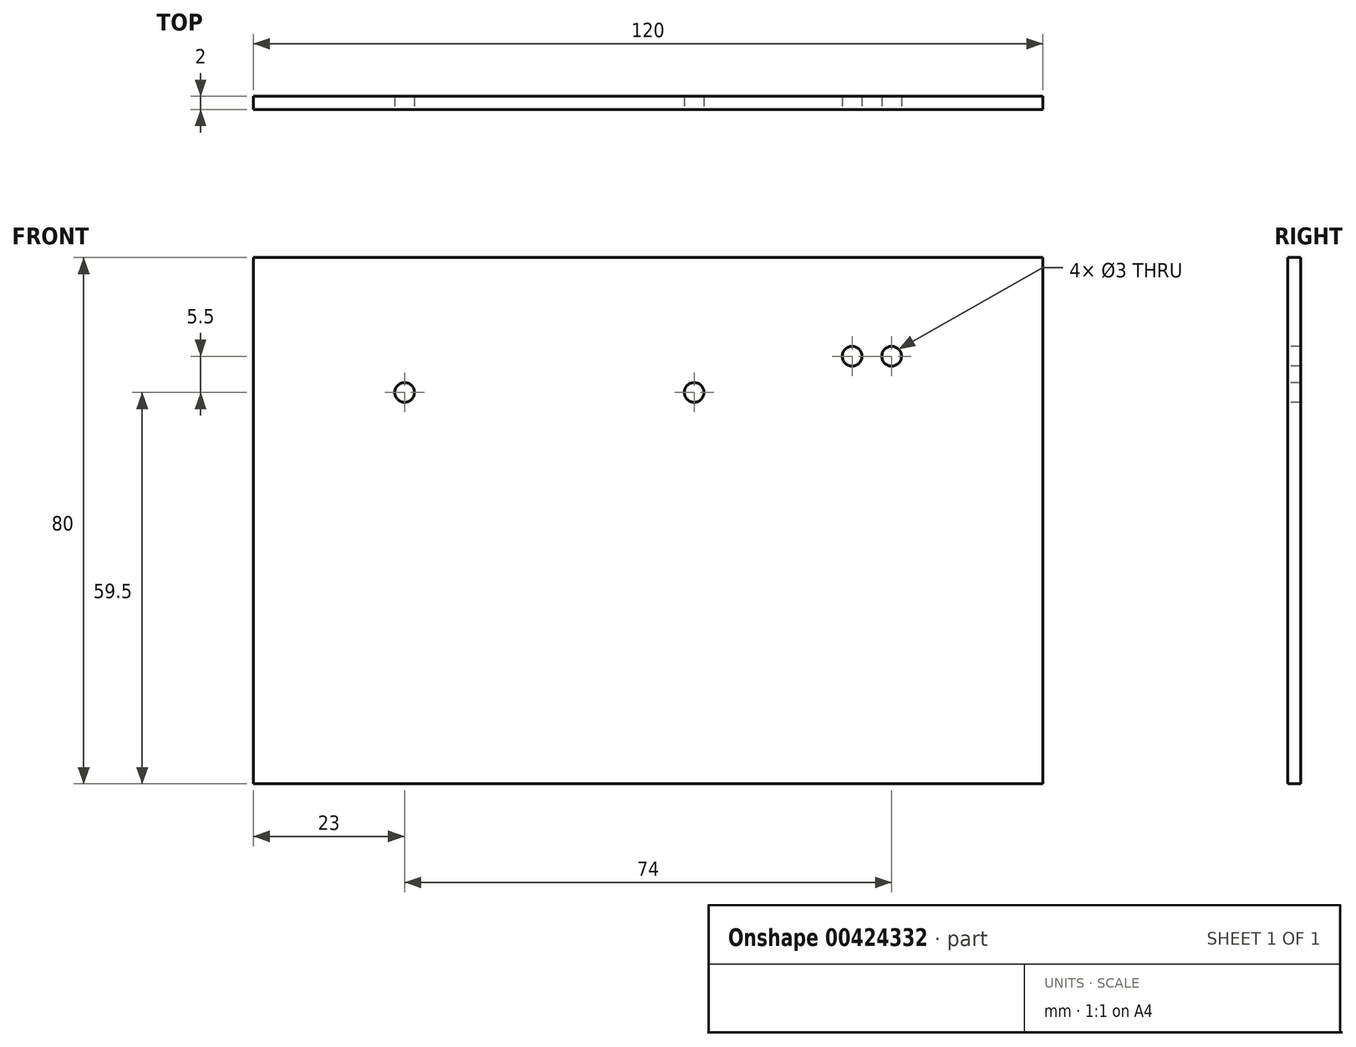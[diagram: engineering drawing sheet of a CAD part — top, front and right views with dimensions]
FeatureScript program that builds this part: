
annotation { "Feature Type Name" : "Feature", "Feature Type Description" : "" }
export const myFeature = defineFeature(function(context is Context, id is Id, definition is map)
    precondition{}
    {
        {
            var Q0;
            Q0=qCreatedBy(makeId("Front.planeOp"),FACE);
            var sketch = newSketch(context, id + "F0", { "sketchPlane" : qUnion([Q0])});
            skLineSegment(sketch, "E0.bottom", {"start": v(0, 0) * mm, "end": v(120, 0) * mm});
            skLineSegment(sketch, "E0.top", {"start": v(0, 80) * mm, "end": v(120, 80) * mm});
            skLineSegment(sketch, "E0.left", {"start": v(0, 0) * mm, "end": v(0, 80) * mm});
            skLineSegment(sketch, "E0.right", {"start": v(120, 0) * mm, "end": v(120, 80) * mm});
            skSolve(sketch);
        }
        {
            var Q0;
            Q0=makeQuery(id+"F0.imprint","IMPRINT",FACE,{"disambiguationData":[TD([[makeQuery(id+"F0.imprint","IMPRINT",EDGE,{"derivedFrom":sQuery(id+"F0.wireOp",EDGE,"E0.bottom")}),1.0]])]});
            extrude(context, id + "F1", {"entities" : qUnion([Q0]), "depth" : 2 * mm});
        }
        {
            var Q0;
            Q0=makeQuery(id+"F1.opExtrude","CAP_FACE",FACE,{"disambiguationData":[OSD([sQuery(id+"F0.wireOp",EDGE,"E0.bottom"),sQuery(id+"F0.wireOp",EDGE,"E0.top"),sQuery(id+"F0.wireOp",EDGE,"E0.left"),sQuery(id+"F0.wireOp",EDGE,"E0.right")])],"isStart":false});
            var sketch = newSketch(context, id + "F2", { "sketchPlane" : qUnion([Q0])});
            skCircle(sketch, "E1", {"center": v(23, 59.5) * mm, "radius": 1.5 * mm});
            skLineSegment(sketch, "E2", {"start": v(0, 40) * mm, "end": v(120, 40) * mm, "construction": true});
            skCircle(sketch, "E3", {"center": v(67, 59.5) * mm, "radius": 1.5 * mm});
            skLineSegment(sketch, "E4", {"start": v(23, 59.5) * mm, "end": v(67, 59.5) * mm});
            skCircle(sketch, "E5", {"center": v(91, 65) * mm, "radius": 1.5 * mm});
            skCircle(sketch, "E6", {"center": v(97, 65) * mm, "radius": 1.5 * mm});
            skLineSegment(sketch, "E7", {"start": v(91, 65) * mm, "end": v(97, 65) * mm});
            skSolve(sketch);
        }
        {
            var Q0;
            Q0 = qSketchRegion(id + "F2", true);
            extrude(context, id + "F3", {"entities" : qUnion([Q0]), "operationType" : NewBodyOperationType.REMOVE, "oppositeDirection" : true, "depth" : 25 * mm});
        }
        {
            var Q0;
            Q0=sQuery(id+"F2.wireOp",EDGE,"E2");
            cPlane(context, id + "F4", {"entities" : qUnion([Q0]), "cplaneType" : CPlaneType.LINE_ANGLE, "offset" : 25 * mm, "angle" : 90 * degree, "width" : 150 * mm, "height" : 150 * mm});
        }
    });
